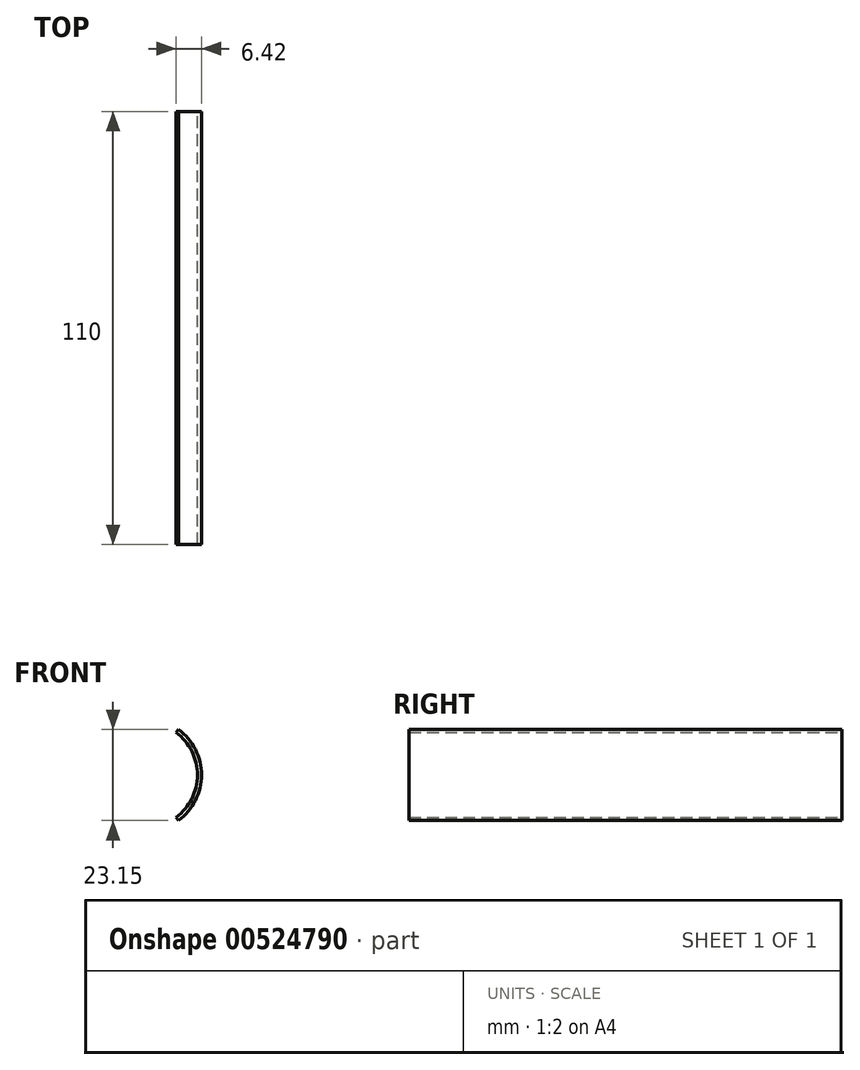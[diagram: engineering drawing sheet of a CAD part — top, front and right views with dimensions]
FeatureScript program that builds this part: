
annotation { "Feature Type Name" : "Feature", "Feature Type Description" : "" }
export const myFeature = defineFeature(function(context is Context, id is Id, definition is map)
    precondition{}
    {
        {
            var Q0;
            Q0=qCreatedBy(makeId("Front.planeOp"),FACE);
            var sketch = newSketch(context, id + "F0", { "sketchPlane" : qUnion([Q0])});
            skArc(sketch, "E0", {"start": v(7.98, -10.76) * mm, "mid": v(13.4, 0) * mm, "end": v(7.98, 10.76) * mm});
            skArc(sketch, "E1.0", {"start": v(8.58, -11.57) * mm, "mid": v(14.4, 0) * mm, "end": v(8.56, 11.58) * mm});
            skLineSegment(sketch, "E2", {"start": v(8.56, 11.58) * mm, "end": v(7.98, 10.76) * mm});
            skLineSegment(sketch, "E3", {"start": v(7.98, -10.76) * mm, "end": v(8.58, -11.57) * mm});
            skPoint(sketch, "E4", {"position": v(13.4, 0) * mm});
            skSolve(sketch);
        }
        {
            var Q0;
            Q0=makeQuery(id+"F0.imprint","IMPRINT",FACE,{"disambiguationData":[TD([[makeQuery(id+"F0.imprint","IMPRINT",EDGE,{"derivedFrom":sQuery(id+"F0.wireOp",EDGE,"E1.0")}),1.0]])]});
            extrude(context, id + "F1", {"entities" : qUnion([Q0]), "endBound" : BoundingType.SYMMETRIC, "depth" : 110 * mm, "offsetDistance" : 25.4 * mm});
        }
    });
